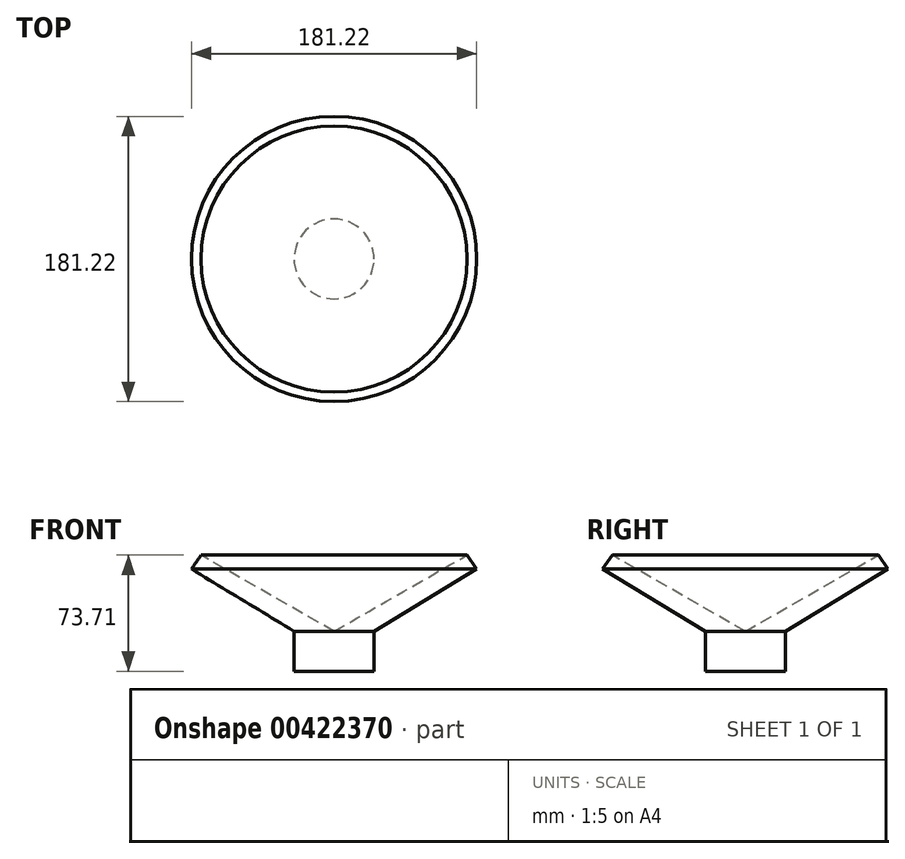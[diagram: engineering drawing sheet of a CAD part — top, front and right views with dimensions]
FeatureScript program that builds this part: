
annotation { "Feature Type Name" : "Feature", "Feature Type Description" : "" }
export const myFeature = defineFeature(function(context is Context, id is Id, definition is map)
    precondition{}
    {
        {
            var Q0;
            Q0=qCreatedBy(makeId("Front.planeOp"),FACE);
            var sketch = newSketch(context, id + "F0", { "sketchPlane" : qUnion([Q0])});
            skLineSegment(sketch, "E0.bottom", {"start": v(0, 0) * mm, "end": v(-25.4, 0) * mm});
            skLineSegment(sketch, "E0.left", {"start": v(0, 0) * mm, "end": v(0, 25.4) * mm});
            skLineSegment(sketch, "E0.right", {"start": v(-25.4, 0) * mm, "end": v(-25.4, 25.4) * mm});
            skLineSegment(sketch, "E1", {"start": v(0, 25.4) * mm, "end": v(65.21, 64.82) * mm});
            skLineSegment(sketch, "E2", {"start": v(-25.4, 25.4) * mm, "end": v(59.08, 73.71) * mm});
            skLineSegment(sketch, "E3", {"start": v(59.08, 73.71) * mm, "end": v(65.21, 64.82) * mm});
            skSolve(sketch);
        }
        {
            var Q0;
            Q0=makeQuery(id+"F0.imprint","IMPRINT",FACE,{"disambiguationData":[TD([[makeQuery(id+"F0.imprint","IMPRINT",EDGE,{"derivedFrom":sQuery(id+"F0.wireOp",EDGE,"E0.bottom")}),-1.0]])]});
            var Q1;
            Q1=sQuery(id+"F0.wireOp",EDGE,"E0.right");
            revolve(context, id + "F1", {"entities" : qUnion([Q0]), "axis" : qUnion([Q1]), "revolveType" : RevolveType.FULL});
        }
    });
